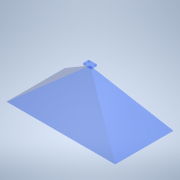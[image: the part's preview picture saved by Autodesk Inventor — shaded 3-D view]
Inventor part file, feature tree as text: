
AUTODESK INVENTOR PART (.ipt)
format: ipt  version: 2022.6 (Build 266554000, 554)  size: 134,144 bytes
history: native  units: mm
features: sketch x6, extrude x2, plane x1, loft x1, hole x1
ambient origin geometry x8: Origin, YZ Plane, XZ Plane, XY Plane, X Axis, Y Axis, Z Axis, Center Point
bodies: Solid1 (feature_tree)
feature tree (11):
  sketch  "Sketch2"  dims[d0=370.5mm d1=198.6mm]
  plane  "Work Plane1"
  loft  "Loft1"
  extrude  "Extrusion1"  TaperAngle=0.0deg  [1 undecoded]
  hole  "Hole1"  [1 undecoded]
  extrude  "Extrusion2"  Depth=5.0mm TaperAngle=0.0deg
  sketch  "Sketch7"  dims[d12=13.0mm d13=3.4mm d14=6.0mm d15=4.0mm d16=2.0mm d17=90.0deg d18=8.0mm d19=20.594885mm d20=2.0mm d21=1.0mm d22=200.0mm d23=0.0mm]
  sketch  "Sketch3"  dims[d2=150.0mm d3=0.0mm d4=90.0deg]
  sketch  "Sketch4"  dims[d5=0.0mm d6=90.0deg d7=28.0mm]
  sketch  "Sketch5"  dims[d8=20.0mm d9=5.0mm d10=0.0mm]
  sketch  "Sketch6"  dims[d11=21.0mm]
note: 2 required parameter values undecoded (feature->parameter linkage not recoverable at this tier; creation-order binding heuristic only, values carry confidence <= 0.55)
